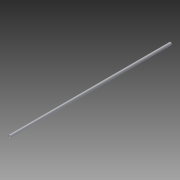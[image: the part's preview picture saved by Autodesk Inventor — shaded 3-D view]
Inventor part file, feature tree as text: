
AUTODESK INVENTOR PART (.ipt)
format: ipt  version: 2013 (Build 170138000, 138)  size: 66,048 bytes
history: native  units: in
note: dims shown in document units (in); Inventor stores cm internally (conversion verified against a paired STEP export)
features: extrude x1, sketch x1
ambient origin geometry x8: Origin, YZ Plane, XZ Plane, XY Plane, X Axis, Y Axis, Z Axis, Center Point
bodies: Solid1 (feature_tree)
feature tree (2):
  extrude  "Extrusion1"  Depth=1.05in
  sketch  "Sketch1"  dims[d0=1.32in d1=1.05in d2=82.5in d3=0.0in]
